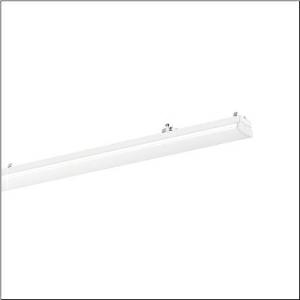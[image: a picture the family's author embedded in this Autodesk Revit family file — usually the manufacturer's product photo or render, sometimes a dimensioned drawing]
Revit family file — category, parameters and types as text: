
# Revit family: licross_r__21_recessed_opal_mo_52te1d7n44xg_bb53
name_source: partatom
category: Lighting Fixtures
units: mm (PartAtom-declared; Revit-internal decimal feet)

## family parameters
Cut with Voids When Loaded = No
Host = Face
Light Source = No
Part Type = Normal
Room Calculation Point = No
Round Connector Dimension = Use Diameter
Shared = No

## types (1)
- Licross® 21 recessed opal MO (1 x LED, 4400 lm, 24.7 W, 4000K)
    Apparent Load = 25 VA
    CIE Flux Codes = 44 73 91 87 100
    Color Rendering = 80
    Color Temperature = 4000K
    Default Elevation = 1800 mm
    Description = Licross® 21 recessed opal MO, luminaire insert, of sheet steel, galvanised, coil coated, white, length: 1.500mm, width: 66mm, height: 67mm, LED rated luminous flux: 4.400lm, light colour: 840, control gear: ON/OFF, with plug, 3-pole, with phase selection, mains connection: 220..240V, AC, 50/60Hz, rated input power: 25W, halogen-free wiring, primary optical cover: cover, of PMMA, light emission: direct with ceiling illumination distribution, primary light characteristic: symmetric, protection rating (complete): IP54, insulation class (complete): insulation class I (protective earthing), certification: CE, ENEC, VDE, UKCA, protection symbol: D if used in an environment with non-conductive dust loads with corresponding accessories, impact resistance: IK06, permissible ambient temperature for indoor applications: -35..+50°C, corresponds to IFS (International Featured Standards) requirements for safety and quality in the food industry, reducing of maximum allowable ambient temperature of 5°C with ceiling mounting, LABS conformity tested according to VDMA 24364:2018-05, packaging unit: 1 piece
    Height = 83 mm
    Lamp = 1 x LED
    Lamp Light Flux = 4400 lm
    Lamp Power = 24.7 W
    Lamp count = 1
    Length = 1500 mm
    Luminous efficacy = 178 lm/W
    Manufacturer = Siteco
    ModVariant = No
    Model = 52TE1D7N44XG
    Mounting Place = Ceiling
    Mounting Type = Pendant
    Number of Poles = 1
    OnlyDefault = Yes
    Power Factor = 1
    Product Name = Licross® 21 recessed opal MO
    Product group = luminaire insert
    ProductGroupID = 902
    Protection Class = Protection class I
    Protection Degree = IP 54
    RLX_Detail_Level = 1
    RLX_Emergency_Light_Flux = 0 lm
    RLX_Emergency_Type = 0
    RLX_Emergency_Type_DB = No
    RlxData = <blob elided: 23205 chars, md5=e74ec897>
    Socket = socket
    Standby Power = 0 W
    System Light Flux = 4400 lm
    System Power = 25 W
    Type Comments = Product without accessories
    Type Image = l_1313666.jpg
    URL = http://relux.com
    VarID = ---
    Voltage = 0 V
    Weight = 0.00 kg
    Width = 76 mm

## geometry (parser evidence)
native form markers: Blend x4, Sweep x13
no freeform markers — native parametric forms only
